# Revit family: SAE106
name_source: partatom
category: Lighting Fixtures
units: mm (PartAtom-declared; Revit-internal decimal feet)

## family parameters
Cut with Voids When Loaded = No
Host = Face
Light Source = Yes
OmniClass Number = 23.80.70.11.14.17
OmniClass Title = Direct/Indirect
Part Type = Normal
Room Calculation Point = No
Round Connector Dimension = Use Diameter
Shared = Yes

## types (2) — shared parameters
Apparent Load = 0 VA
Assembly Code = D5020200
Color Filter = 16777215
Default Elevation = 4' - 0"
Description = Linear Pendant Indirect/Direct
Dimming Lamp Color Temperature Shift = <None>
Emit Shape Visible in Rendering = No
Emit from Rectangle Width = 0' - 4"
Glass = White Glass
Housing Material = Paint -  Matte White
Lamp = LED's
Load Classification = Lighting
Manufacturer = Litecontrol
Model = SAE106
Photometric Notes = More IES files download on Photometric Web Link
Photometric Web File = SAE106-P-4-SOF-35K-155-10D.IES
Power Factor = 1
Tilt Angle = -90.00°
URL = https://www.currentlighting.com
Voltage = 120 V
Warranty = 5-Years Warranty
Wattage Comments = Up to 133 lumens/watt efficacy

## per-type parameters (varying)
| type | Emit from Rectangle Length | zz Length 1 |
| SAE106-04 | 3' - 10" | 4' - 0" |
| SAE106-08 | 7' - 10" | 8' - 0" |

## geometry (parser evidence)
native form markers: Sweep x6
no freeform markers — native parametric forms only
